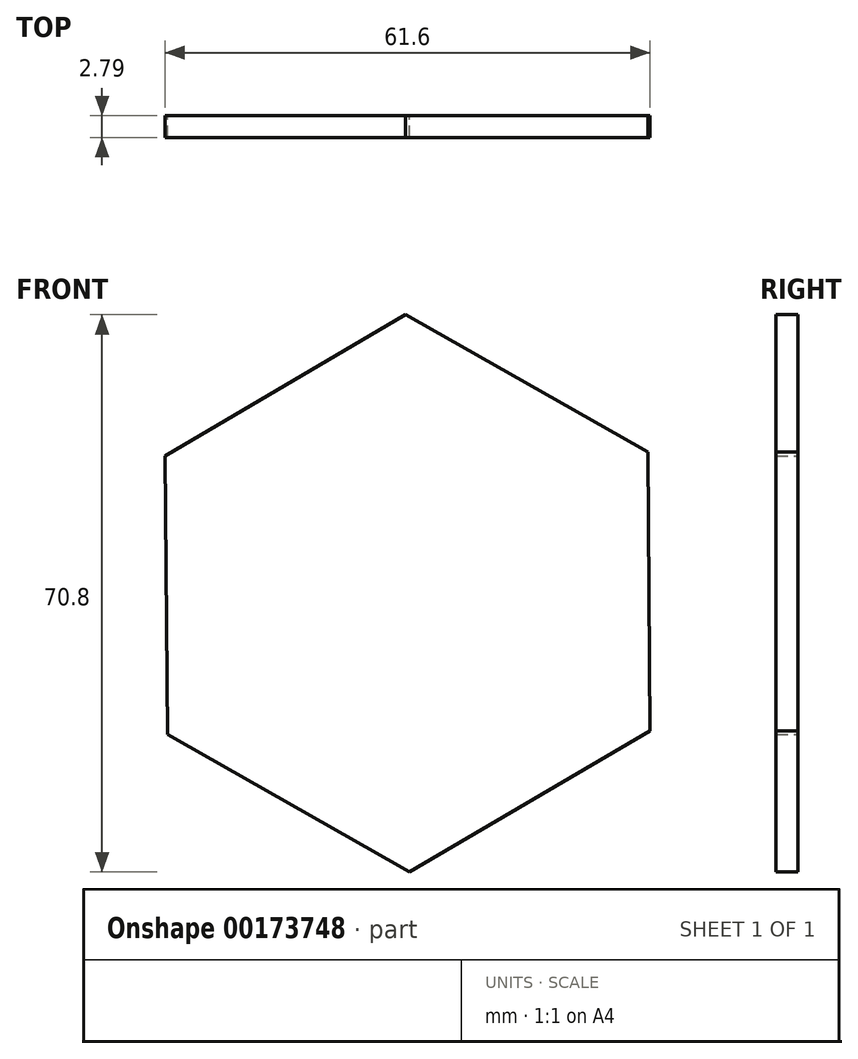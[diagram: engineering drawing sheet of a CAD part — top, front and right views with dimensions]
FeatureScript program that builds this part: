
annotation { "Feature Type Name" : "Feature", "Feature Type Description" : "" }
export const myFeature = defineFeature(function(context is Context, id is Id, definition is map)
    precondition{}
    {
        {
            var Q0;
            Q0=qCreatedBy(makeId("Front.planeOp"),FACE);
            var sketch = newSketch(context, id + "F0", { "sketchPlane" : qUnion([Q0])});
            skCircle(sketch, "E0.cCircle", {"center": v(0, 0) * mm, "radius": 30.66 * mm, "construction": true});
            skLineSegment(sketch, "E0.0", {"start": v(-0.28, 35.4) * mm, "end": v(30.52, 17.94) * mm});
            skLineSegment(sketch, "E0.1", {"start": v(30.52, 17.94) * mm, "end": v(30.8, -17.46) * mm});
            skLineSegment(sketch, "E0.2", {"start": v(30.8, -17.46) * mm, "end": v(0.28, -35.4) * mm});
            skLineSegment(sketch, "E0.3", {"start": v(0.28, -35.4) * mm, "end": v(-30.52, -17.94) * mm});
            skLineSegment(sketch, "E0.4", {"start": v(-30.52, -17.94) * mm, "end": v(-30.8, 17.46) * mm});
            skLineSegment(sketch, "E0.5", {"start": v(-30.8, 17.46) * mm, "end": v(-0.28, 35.4) * mm});
            skPoint(sketch, "E0.0.midPoint", {"position": v(15.12, 26.67) * mm});
            skCircle(sketch, "E1", {"center": v(0, 0) * mm, "radius": 13.65 * mm});
            skSolve(sketch);
        }
        {
            var Q0;
            Q0 = qSketchRegion(id + "F0", true);
            var Q1;
            Q1=makeQuery(id+"F0.imprint","IMPRINT",FACE,{"disambiguationData":[TD([[makeQuery(id+"F0.imprint","IMPRINT",EDGE,{"derivedFrom":sQuery(id+"F0.wireOp",EDGE,"E1")}),1.0]])]});
            extrude(context, id + "F1", {"entities" : qUnion([Q0, Q1]), "depth" : 2.8 * mm});
        }
    });
